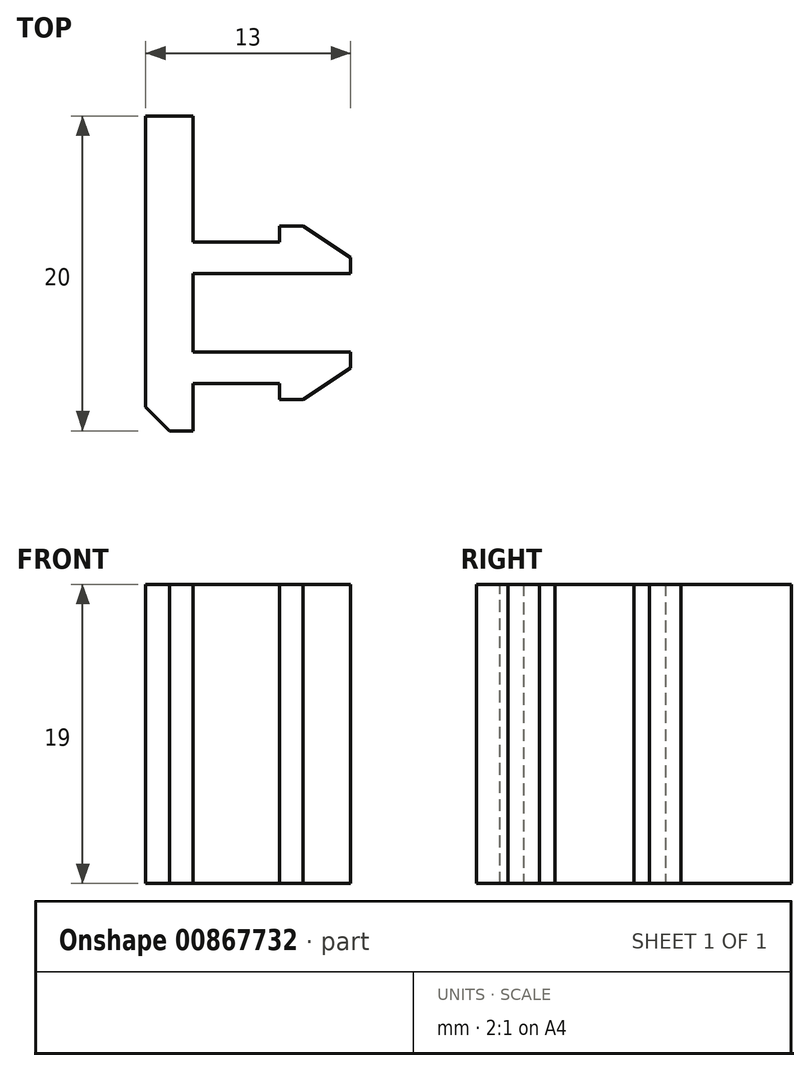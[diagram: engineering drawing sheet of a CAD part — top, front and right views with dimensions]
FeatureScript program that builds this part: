
annotation { "Feature Type Name" : "Feature", "Feature Type Description" : "" }
export const myFeature = defineFeature(function(context is Context, id is Id, definition is map)
    precondition{}
    {
        {
            var Q0;
            Q0=qCreatedBy(makeId("Top.planeOp"),FACE);
            var sketch = newSketch(context, id + "F0", { "sketchPlane" : qUnion([Q0])});
            skLineSegment(sketch, "E0", {"start": v(0, 0) * mm, "end": v(0, 20) * mm});
            skLineSegment(sketch, "E1", {"start": v(0, 20) * mm, "end": v(3, 20) * mm});
            skLineSegment(sketch, "E2", {"start": v(3, 20) * mm, "end": v(3, 12) * mm});
            skLineSegment(sketch, "E3", {"start": v(3, 0) * mm, "end": v(0, 0) * mm});
            skLineSegment(sketch, "E4", {"start": v(3, 3) * mm, "end": v(8.5, 3) * mm});
            skLineSegment(sketch, "E5", {"start": v(8.5, 3) * mm, "end": v(8.5, 2) * mm});
            skLineSegment(sketch, "E6", {"start": v(8.5, 2) * mm, "end": v(10, 2) * mm});
            skLineSegment(sketch, "E7", {"start": v(10, 2) * mm, "end": v(13, 4) * mm});
            skLineSegment(sketch, "E8", {"start": v(13, 4) * mm, "end": v(13, 5) * mm});
            skLineSegment(sketch, "E9", {"start": v(13, 5) * mm, "end": v(3, 5) * mm});
            skLineSegment(sketch, "E10", {"start": v(3, 5) * mm, "end": v(3, 10) * mm});
            skLineSegment(sketch, "E11", {"start": v(3, 10) * mm, "end": v(13, 10) * mm});
            skLineSegment(sketch, "E12", {"start": v(13, 10) * mm, "end": v(13, 11) * mm});
            skLineSegment(sketch, "E13", {"start": v(13, 11) * mm, "end": v(10, 13) * mm});
            skLineSegment(sketch, "E14", {"start": v(10, 13) * mm, "end": v(8.5, 13) * mm});
            skLineSegment(sketch, "E15", {"start": v(8.5, 13) * mm, "end": v(8.5, 12) * mm});
            skLineSegment(sketch, "E16", {"start": v(8.5, 12) * mm, "end": v(3, 12) * mm});
            skLineSegment(sketch, "E17.trimOffspring", {"start": v(3, 10) * mm, "end": v(3, 5) * mm});
            skLineSegment(sketch, "E18.trimOffspring", {"start": v(3, 3) * mm, "end": v(3, 0) * mm});
            skSolve(sketch);
        }
        {
            var Q0;
            Q0=makeQuery(id+"F0.imprint","IMPRINT",FACE,{"disambiguationData":[TD([[makeQuery(id+"F0.imprint","IMPRINT",EDGE,{"derivedFrom":sQuery(id+"F0.wireOp",EDGE,"E0")}),-1.0]])]});
            extrude(context, id + "F1", {"entities" : qUnion([Q0]), "depth" : 19 * mm, "offsetDistance" : 25 * mm});
        }
        {
            var Q0;
            Q0=makeQuery(id+"F1.opExtrude","SWEPT_EDGE",EDGE,{"disambiguationData":[OSD([sQuery(id+"F0.wireOp",EDGE,"E0"),sQuery(id+"F0.wireOp",EDGE,"E3")])]});
            chamfer(context, id + "F2", {"entities" : qUnion([Q0]), "width" : 1.5 * mm, "tangentPropagation" : true});
        }
    });
